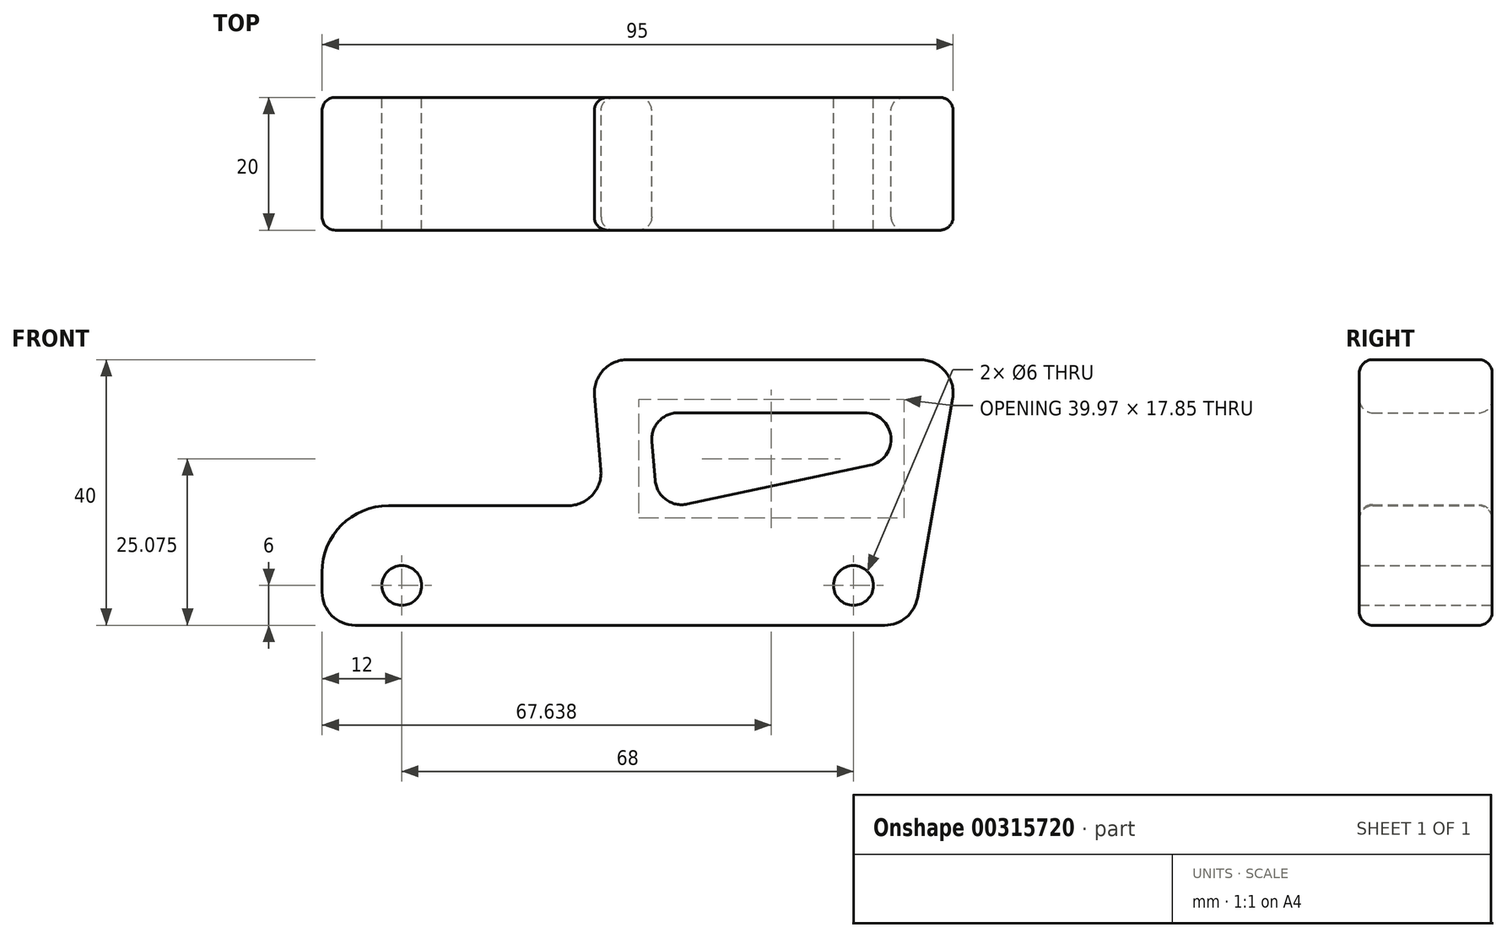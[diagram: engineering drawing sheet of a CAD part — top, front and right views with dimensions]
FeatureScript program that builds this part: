
annotation { "Feature Type Name" : "Feature", "Feature Type Description" : "" }
export const myFeature = defineFeature(function(context is Context, id is Id, definition is map)
    precondition{}
    {
        {
            var Q0;
            Q0=qCreatedBy(makeId("Front.planeOp"),FACE);
            var sketch = newSketch(context, id + "F0", { "sketchPlane" : qUnion([Q0])});
            skLineSegment(sketch, "E0.bottom", {"start": v(0, 0) * mm, "end": v(95, 0) * mm});
            skLineSegment(sketch, "E0.top", {"start": v(0, 40) * mm, "end": v(95, 40) * mm});
            skLineSegment(sketch, "E0.left", {"start": v(0, 0) * mm, "end": v(0, 40) * mm});
            skLineSegment(sketch, "E0.right", {"start": v(95, 0) * mm, "end": v(95, 40) * mm});
            skLineSegment(sketch, "E1", {"start": v(41, 34.56) * mm, "end": v(41.98, 23.44) * mm});
            skLineSegment(sketch, "E2", {"start": v(37, 18) * mm, "end": v(10, 18) * mm});
            skLineSegment(sketch, "E3", {"start": v(0, 8) * mm, "end": v(0, 5) * mm});
            skLineSegment(sketch, "E4", {"start": v(5, 0) * mm, "end": v(84.71, 0) * mm});
            skLineSegment(sketch, "E5", {"start": v(90, 40) * mm, "end": v(45.99, 40) * mm});
            skArc(sketch, "E6", {"start": v(41.98, 23.44) * mm, "mid": v(40.69, 19.62) * mm, "end": v(37, 18) * mm});
            skArc(sketch, "E7", {"start": v(10, 18) * mm, "mid": v(2.93, 15.07) * mm, "end": v(0, 8) * mm});
            skArc(sketch, "E8", {"start": v(0, 5) * mm, "mid": v(1.46, 1.46) * mm, "end": v(5, 0) * mm});
            skArc(sketch, "E9", {"start": v(84.71, 0) * mm, "mid": v(87.92, 1.17) * mm, "end": v(89.63, 4.13) * mm});
            skArc(sketch, "E10", {"start": v(94.92, 34.13) * mm, "mid": v(93.83, 38.21) * mm, "end": v(90, 40) * mm});
            skArc(sketch, "E11", {"start": v(45.99, 40) * mm, "mid": v(42.3, 38.38) * mm, "end": v(41, 34.56) * mm});
            skLineSegment(sketch, "E12", {"start": v(89.63, 4.13) * mm, "end": v(94.92, 34.13) * mm});
            skLineSegment(sketch, "E13", {"start": v(53.63, 32) * mm, "end": v(81.66, 32) * mm});
            skLineSegment(sketch, "E14", {"start": v(54.97, 18.24) * mm, "end": v(82.49, 24.09) * mm});
            skArc(sketch, "E15", {"start": v(81.66, 32) * mm, "mid": v(85.64, 28.42) * mm, "end": v(82.49, 24.09) * mm});
            skLineSegment(sketch, "E16", {"start": v(49.64, 27.65) * mm, "end": v(50.15, 21.8) * mm});
            skArc(sketch, "E17", {"start": v(53.63, 32) * mm, "mid": v(50.68, 30.7) * mm, "end": v(49.64, 27.65) * mm});
            skArc(sketch, "E18", {"start": v(50.15, 21.8) * mm, "mid": v(51.76, 18.94) * mm, "end": v(54.97, 18.24) * mm});
            skSolve(sketch);
        }
        {
            var Q0;
            Q0=makeQuery(id+"F0.imprint","IMPRINT",FACE,{"disambiguationData":[TD([[makeQuery(id+"F0.imprint","IMPRINT",EDGE,{"derivedFrom":sQuery(id+"F0.wireOp",EDGE,"E1")}),1.0]])]});
            extrude(context, id + "F1", {"entities" : qUnion([Q0]), "depth" : 20 * mm});
        }
        {
            var Q0;
            Q0=makeQuery(id+"F1.opExtrude","CAP_EDGE",EDGE,{"disambiguationData":[OSD([sQuery(id+"F0.wireOp",EDGE,"E13")])],"isStart":false});
            var Q1;
            Q1=makeQuery(id+"F1.opExtrude","CAP_EDGE",EDGE,{"disambiguationData":[OSD([sQuery(id+"F0.wireOp",EDGE,"E1")])],"isStart":false});
            var Q2;
            Q2=makeQuery(id+"F1.opExtrude","CAP_EDGE",EDGE,{"disambiguationData":[OSD([sQuery(id+"F0.wireOp",EDGE,"E14")])],"isStart":true});
            var Q3;
            Q3=makeQuery(id+"F1.opExtrude","CAP_EDGE",EDGE,{"disambiguationData":[OSD([sQuery(id+"F0.wireOp",EDGE,"E1")])],"isStart":true});
            fillet(context, id + "F2", {"entities" : qUnion([Q0, Q1, Q2, Q3]), "radius" : 2 * mm, "tangentPropagation" : true, "allowEdgeOverflow" : false});
        }
        {
            var Q0;
            Q0=qCreatedBy(makeId("Front.planeOp"),FACE);
            var sketch = newSketch(context, id + "F3", { "sketchPlane" : qUnion([Q0])});
            skPoint(sketch, "E19", {"position": v(12, 6) * mm});
            skPoint(sketch, "E20", {"position": v(80, 6) * mm});
            skSolve(sketch);
        }
        {
            var Q0;
            Q0=sQuery(id+"F3.wireOp",VERTEX,"E19");
            var Q1;
            Q1=sQuery(id+"F3.wireOp",VERTEX,"E20");
            var Q2;
            Q2=makeQuery(id+"F1.opExtrude","SWEPT_BODY",BODY,{"disambiguationData":[OSD([sQuery(id+"F0.wireOp",EDGE,"E1"),sQuery(id+"F0.wireOp",EDGE,"E2"),sQuery(id+"F0.wireOp",EDGE,"E3"),sQuery(id+"F0.wireOp",EDGE,"E4"),sQuery(id+"F0.wireOp",EDGE,"E5"),sQuery(id+"F0.wireOp",EDGE,"E6"),sQuery(id+"F0.wireOp",EDGE,"E7"),sQuery(id+"F0.wireOp",EDGE,"E8"),sQuery(id+"F0.wireOp",EDGE,"E9"),sQuery(id+"F0.wireOp",EDGE,"E10"),sQuery(id+"F0.wireOp",EDGE,"E11"),sQuery(id+"F0.wireOp",EDGE,"E12"),sQuery(id+"F0.wireOp",EDGE,"E13"),sQuery(id+"F0.wireOp",EDGE,"E14"),sQuery(id+"F0.wireOp",EDGE,"E15"),sQuery(id+"F0.wireOp",EDGE,"E16"),sQuery(id+"F0.wireOp",EDGE,"E17"),sQuery(id+"F0.wireOp",EDGE,"E18")])]});
            hole(context, id + "F4", {"style" : HoleStyle.SIMPLE, "endStyle" : HoleEndStyle.THROUGH, "oppositeDirection" : true, "holeDiameter" : 6 * mm, "tappedDepth" : 12 * mm, "tapClearance" : 3, "locations" : qUnion([Q0, Q1]), "scope" : qUnion([Q2])});
        }
    });
